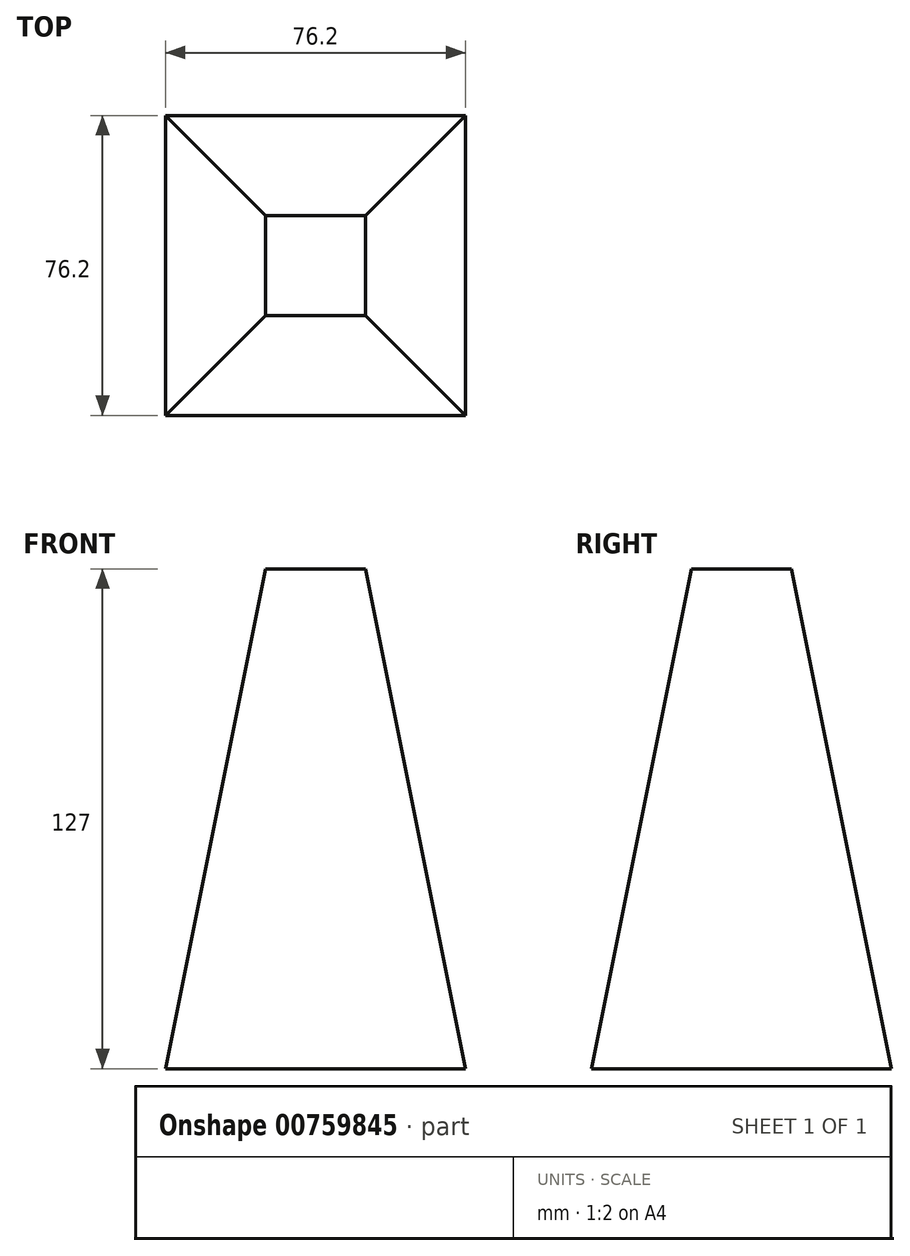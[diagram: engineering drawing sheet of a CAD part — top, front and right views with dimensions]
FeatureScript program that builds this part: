
annotation { "Feature Type Name" : "Feature", "Feature Type Description" : "" }
export const myFeature = defineFeature(function(context is Context, id is Id, definition is map)
    precondition{}
    {
        {
            var Q0;
            Q0=qCreatedBy(makeId("Front.planeOp"),FACE);
            var sketch = newSketch(context, id + "F0", { "sketchPlane" : qUnion([Q0])});
            skLineSegment(sketch, "E0.bottom", {"start": v(0, 0) * mm, "end": v(76.2, 0) * mm});
            skLineSegment(sketch, "E0.top", {"start": v(0, 127) * mm, "end": v(76.2, 127) * mm});
            skLineSegment(sketch, "E0.left", {"start": v(0, 0) * mm, "end": v(0, 127) * mm});
            skLineSegment(sketch, "E0.right", {"start": v(76.2, 0) * mm, "end": v(76.2, 127) * mm});
            skSolve(sketch);
        }
        {
            var Q0;
            Q0=makeQuery(id+"F0.imprint","IMPRINT",FACE,{"disambiguationData":[TD([[makeQuery(id+"F0.imprint","IMPRINT",EDGE,{"derivedFrom":sQuery(id+"F0.wireOp",EDGE,"E0.bottom")}),1.0]])]});
            extrude(context, id + "F1", {"entities" : qUnion([Q0]), "depth" : 76.2 * mm, "offsetDistance" : 25.4 * mm});
        }
        {
            var Q0;
            Q0=makeQuery(id+"F1.opExtrude","SWEPT_FACE",FACE,{"disambiguationData":[OSD([sQuery(id+"F0.wireOp",EDGE,"E0.left")])]});
            var sketch = newSketch(context, id + "F2", { "sketchPlane" : qUnion([Q0])});
            skLineSegment(sketch, "E1", {"start": v(0, 0) * mm, "end": v(25.4, 127) * mm});
            skLineSegment(sketch, "E2", {"start": v(76.2, 0) * mm, "end": v(50.8, 127) * mm});
            skLineSegment(sketch, "E3", {"start": v(0, 0) * mm, "end": v(0, 127) * mm});
            skLineSegment(sketch, "E4", {"start": v(0, 127) * mm, "end": v(25.4, 127) * mm});
            skLineSegment(sketch, "E5", {"start": v(50.8, 127) * mm, "end": v(76.2, 127) * mm});
            skLineSegment(sketch, "E6", {"start": v(76.2, 127) * mm, "end": v(76.2, 0) * mm});
            skSolve(sketch);
        }
        {
            var Q0;
            Q0=makeQuery(id+"F2.imprint","IMPRINT",FACE,{"disambiguationData":[TD([[makeQuery(id+"F2.imprint","IMPRINT",EDGE,{"derivedFrom":sQuery(id+"F2.wireOp",EDGE,"E1")}),1.0]])]});
            var Q1;
            Q1=makeQuery(id+"F2.imprint","IMPRINT",FACE,{"disambiguationData":[TD([[makeQuery(id+"F2.imprint","IMPRINT",EDGE,{"derivedFrom":sQuery(id+"F2.wireOp",EDGE,"E2")}),-1.0]])]});
            extrude(context, id + "F3", {"entities" : qUnion([Q0, Q1]), "operationType" : NewBodyOperationType.REMOVE, "oppositeDirection" : true, "depth" : 76.2 * mm, "offsetDistance" : 25.4 * mm});
        }
        {
            var Q0;
            Q0=qCreatedBy(makeId("Front.planeOp"),FACE);
            var sketch = newSketch(context, id + "F4", { "sketchPlane" : qUnion([Q0])});
            skLineSegment(sketch, "E7", {"start": v(0, 0) * mm, "end": v(25.4, 127) * mm});
            skLineSegment(sketch, "E8", {"start": v(76.2, 0) * mm, "end": v(50.8, 127) * mm});
            skLineSegment(sketch, "E9", {"start": v(50.8, 127) * mm, "end": v(76.2, 127) * mm});
            skLineSegment(sketch, "E10", {"start": v(76.2, 127) * mm, "end": v(76.2, 0) * mm});
            skLineSegment(sketch, "E11", {"start": v(0, 0) * mm, "end": v(0, 127) * mm});
            skLineSegment(sketch, "E12", {"start": v(0, 127) * mm, "end": v(25.4, 127) * mm});
            skSolve(sketch);
        }
        {
            var Q0;
            Q0=makeQuery(id+"F4.imprint","IMPRINT",FACE,{"disambiguationData":[TD([[makeQuery(id+"F4.imprint","IMPRINT",EDGE,{"derivedFrom":sQuery(id+"F4.wireOp",EDGE,"E7")}),1.0]])]});
            var Q1;
            Q1=makeQuery(id+"F4.imprint","IMPRINT",FACE,{"disambiguationData":[TD([[makeQuery(id+"F4.imprint","IMPRINT",EDGE,{"derivedFrom":sQuery(id+"F4.wireOp",EDGE,"E8")}),-1.0]])]});
            extrude(context, id + "F5", {"entities" : qUnion([Q0, Q1]), "operationType" : NewBodyOperationType.REMOVE, "depth" : 76.2 * mm, "offsetDistance" : 25.4 * mm});
        }
    });
